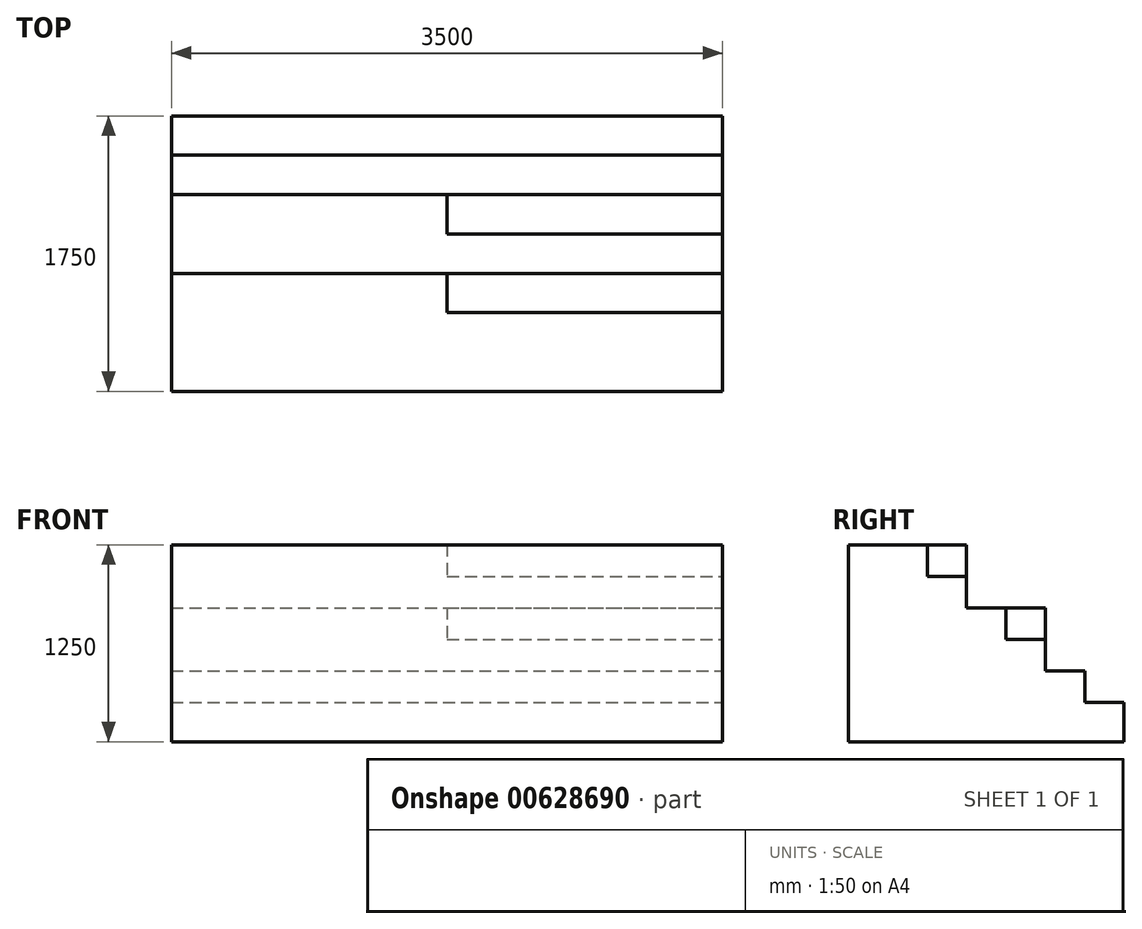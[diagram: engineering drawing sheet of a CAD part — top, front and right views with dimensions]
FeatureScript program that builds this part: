
annotation { "Feature Type Name" : "Feature", "Feature Type Description" : "" }
export const myFeature = defineFeature(function(context is Context, id is Id, definition is map)
    precondition{}
    {
        {
            var Q0;
            Q0=qCreatedBy(makeId("Top.planeOp"),FACE);
            var sketch = newSketch(context, id + "F0", { "sketchPlane" : qUnion([Q0])});
            skLineSegment(sketch, "E0.bottom", {"start": v(0, 0) * mm, "end": v(3500, 0) * mm});
            skLineSegment(sketch, "E0.top", {"start": v(0, 1500) * mm, "end": v(3500, 1500) * mm});
            skLineSegment(sketch, "E0.left", {"start": v(0, 0) * mm, "end": v(0, 1500) * mm});
            skLineSegment(sketch, "E0.right", {"start": v(3500, 0) * mm, "end": v(3500, 1500) * mm});
            skSolve(sketch);
        }
        {
            var Q0;
            Q0=makeQuery(id+"F0.imprint","IMPRINT",FACE,{"disambiguationData":[TD([[makeQuery(id+"F0.imprint","IMPRINT",EDGE,{"derivedFrom":sQuery(id+"F0.wireOp",EDGE,"E0.bottom")}),1.0]])]});
            extrude(context, id + "F1", {"entities" : qUnion([Q0]), "depth" : 250 * mm, "offsetDistance" : 25 * mm});
        }
        {
            var Q0;
            Q0=makeQuery(id+"F1.opExtrude","CAP_FACE",FACE,{"disambiguationData":[OSD([sQuery(id+"F0.wireOp",EDGE,"E0.bottom"),sQuery(id+"F0.wireOp",EDGE,"E0.top"),sQuery(id+"F0.wireOp",EDGE,"E0.left"),sQuery(id+"F0.wireOp",EDGE,"E0.right")])],"isStart":false});
            var sketch = newSketch(context, id + "F2", { "sketchPlane" : qUnion([Q0])});
            skLineSegment(sketch, "E1.bottom", {"start": v(0, 0) * mm, "end": v(3500, 0) * mm});
            skLineSegment(sketch, "E1.top", {"start": v(0, 1250) * mm, "end": v(3500, 1250) * mm});
            skLineSegment(sketch, "E1.left", {"start": v(0, 0) * mm, "end": v(0, 1250) * mm});
            skLineSegment(sketch, "E1.right", {"start": v(3500, 0) * mm, "end": v(3500, 1250) * mm});
            skLineSegment(sketch, "E2.bottom", {"start": v(0, 1250) * mm, "end": v(1750, 1250) * mm});
            skLineSegment(sketch, "E2.top", {"start": v(0, 1500) * mm, "end": v(1750, 1500) * mm});
            skLineSegment(sketch, "E2.left", {"start": v(0, 1250) * mm, "end": v(0, 1500) * mm});
            skLineSegment(sketch, "E2.right", {"start": v(1750, 1250) * mm, "end": v(1750, 1500) * mm});
            skSolve(sketch);
        }
        {
            var Q0;
            Q0=makeQuery(id+"F2.imprint","IMPRINT",FACE,{"disambiguationData":[TD([[makeQuery(id+"F2.imprint","IMPRINT",EDGE,{"derivedFrom":sQuery(id+"F2.wireOp",EDGE,"E1.bottom")}),1.0]])]});
            var Q1;
            Q1=makeQuery(id+"F2.imprint","IMPRINT",FACE,{"disambiguationData":[TD([[makeQuery(id+"F2.imprint","IMPRINT",EDGE,{"derivedFrom":sQuery(id+"F2.wireOp",EDGE,"E2.bottom")}),1.0]])]});
            extrude(context, id + "F3", {"entities" : qUnion([Q0, Q1]), "operationType" : NewBodyOperationType.ADD, "depth" : 200 * mm, "offsetDistance" : 25 * mm});
        }
        {
            var Q0;
            Q0=makeQuery(id+"F3.opExtrude","CAP_FACE",FACE,{"disambiguationData":[OSD([sQuery(id+"F2.wireOp",EDGE,"E1.bottom"),sQuery(id+"F2.wireOp",EDGE,"E1.top"),sQuery(id+"F2.wireOp",EDGE,"E1.left"),sQuery(id+"F2.wireOp",EDGE,"E1.right")])],"isStart":false});
            var sketch = newSketch(context, id + "F4", { "sketchPlane" : qUnion([Q0])});
            skLineSegment(sketch, "E3.bottom", {"start": v(0, 0) * mm, "end": v(1750, 0) * mm});
            skLineSegment(sketch, "E3.top", {"start": v(0, 500) * mm, "end": v(1750, 500) * mm});
            skLineSegment(sketch, "E3.left", {"start": v(0, 0) * mm, "end": v(0, 500) * mm});
            skLineSegment(sketch, "E3.right", {"start": v(1750, 0) * mm, "end": v(1750, 500) * mm});
            skLineSegment(sketch, "E4.bottom", {"start": v(1750, 0) * mm, "end": v(3500, 0) * mm});
            skLineSegment(sketch, "E4.top", {"start": v(1750, 250) * mm, "end": v(3500, 250) * mm});
            skLineSegment(sketch, "E4.left", {"start": v(1750, 0) * mm, "end": v(1750, 250) * mm});
            skLineSegment(sketch, "E4.right", {"start": v(3500, 0) * mm, "end": v(3500, 250) * mm});
            skLineSegment(sketch, "E5.left", {"start": v(1750, 500) * mm, "end": v(1750, 250) * mm});
            skSolve(sketch);
        }
        {
            var Q0;
            Q0 = qSketchRegion(id + "F4", true);
            extrude(context, id + "F5", {"entities" : qUnion([Q0]), "operationType" : NewBodyOperationType.ADD, "depth" : 800 * mm, "offsetDistance" : 25 * mm});
        }
        {
            var Q0;
            Q0=makeQuery(id+"F3.opExtrude","CAP_FACE",FACE,{"disambiguationData":[OSD([sQuery(id+"F2.wireOp",EDGE,"E1.bottom"),sQuery(id+"F2.wireOp",EDGE,"E1.top"),sQuery(id+"F2.wireOp",EDGE,"E1.left"),sQuery(id+"F2.wireOp",EDGE,"E1.right")])],"isStart":false});
            var sketch = newSketch(context, id + "F6", { "sketchPlane" : qUnion([Q0])});
            skLineSegment(sketch, "E6.bottom", {"start": v(1750, 500) * mm, "end": v(3500, 500) * mm});
            skLineSegment(sketch, "E6.top", {"start": v(1750, 250) * mm, "end": v(3500, 250) * mm});
            skLineSegment(sketch, "E6.left", {"start": v(1750, 500) * mm, "end": v(1750, 250) * mm});
            skLineSegment(sketch, "E6.right", {"start": v(3500, 500) * mm, "end": v(3500, 250) * mm});
            skSolve(sketch);
        }
        {
            var Q0;
            Q0=makeQuery(id+"F6.imprint","IMPRINT",FACE,{"disambiguationData":[TD([[makeQuery(id+"F6.imprint","IMPRINT",EDGE,{"derivedFrom":sQuery(id+"F6.wireOp",EDGE,"E6.bottom")}),-1.0]])]});
            extrude(context, id + "F7", {"entities" : qUnion([Q0]), "operationType" : NewBodyOperationType.ADD, "depth" : 600 * mm, "offsetDistance" : 25 * mm});
        }
        {
            var Q0;
            Q0=makeQuery(id+"F3.opExtrude","CAP_FACE",FACE,{"disambiguationData":[OSD([sQuery(id+"F2.wireOp",EDGE,"E1.bottom"),sQuery(id+"F2.wireOp",EDGE,"E1.top"),sQuery(id+"F2.wireOp",EDGE,"E1.left"),sQuery(id+"F2.wireOp",EDGE,"E1.right")])],"isStart":false});
            var sketch = newSketch(context, id + "F8", { "sketchPlane" : qUnion([Q0])});
            skLineSegment(sketch, "E7.bottom", {"start": v(0, 1000) * mm, "end": v(1750, 1000) * mm});
            skLineSegment(sketch, "E7.top", {"start": v(0, 500) * mm, "end": v(1750, 500) * mm});
            skLineSegment(sketch, "E7.left", {"start": v(0, 1000) * mm, "end": v(0, 500) * mm});
            skLineSegment(sketch, "E7.right", {"start": v(1750, 1000) * mm, "end": v(1750, 500) * mm});
            skLineSegment(sketch, "E8.bottom", {"start": v(1750, 750) * mm, "end": v(3500, 750) * mm});
            skLineSegment(sketch, "E8.top", {"start": v(1750, 500) * mm, "end": v(3500, 500) * mm});
            skLineSegment(sketch, "E8.left", {"start": v(1750, 750) * mm, "end": v(1750, 500) * mm});
            skLineSegment(sketch, "E8.right", {"start": v(3500, 750) * mm, "end": v(3500, 500) * mm});
            skSolve(sketch);
        }
        {
            var Q0;
            Q0 = qSketchRegion(id + "F8", true);
            extrude(context, id + "F9", {"entities" : qUnion([Q0]), "operationType" : NewBodyOperationType.ADD, "depth" : 400 * mm, "offsetDistance" : 25 * mm});
        }
        {
            var Q0;
            Q0=makeQuery(id+"F3.opExtrude","CAP_FACE",FACE,{"disambiguationData":[OSD([sQuery(id+"F2.wireOp",EDGE,"E1.bottom"),sQuery(id+"F2.wireOp",EDGE,"E1.top"),sQuery(id+"F2.wireOp",EDGE,"E1.left"),sQuery(id+"F2.wireOp",EDGE,"E1.right")])],"isStart":false});
            var sketch = newSketch(context, id + "F10", { "sketchPlane" : qUnion([Q0])});
            skLineSegment(sketch, "E9.bottom", {"start": v(1750, 1000) * mm, "end": v(3500, 1000) * mm});
            skLineSegment(sketch, "E9.top", {"start": v(1750, 750) * mm, "end": v(3500, 750) * mm});
            skLineSegment(sketch, "E9.left", {"start": v(1750, 1000) * mm, "end": v(1750, 750) * mm});
            skLineSegment(sketch, "E9.right", {"start": v(3500, 1000) * mm, "end": v(3500, 750) * mm});
            skSolve(sketch);
        }
        {
            var Q0;
            Q0=makeQuery(id+"F10.imprint","IMPRINT",FACE,{"disambiguationData":[TD([[makeQuery(id+"F10.imprint","IMPRINT",EDGE,{"derivedFrom":sQuery(id+"F10.wireOp",EDGE,"E9.bottom")}),-1.0]])]});
            extrude(context, id + "F11", {"entities" : qUnion([Q0]), "operationType" : NewBodyOperationType.ADD, "depth" : 200 * mm, "offsetDistance" : 25 * mm});
        }
        {
            var Q0;
            Q0=makeQuery(id+"F5.boolean.opBoolean","MERGE",FACE,{"derivedFrom":[makeQuery(id+"F3.boolean.opBoolean","MERGE",FACE,{"derivedFrom":[makeQuery(id+"F1.opExtrude","SWEPT_FACE",FACE,{"disambiguationData":[OSD([sQuery(id+"F0.wireOp",EDGE,"E0.bottom")])]}),makeQuery(id+"F3.opExtrude","SWEPT_FACE",FACE,{"disambiguationData":[OSD([sQuery(id+"F2.wireOp",EDGE,"E1.bottom")])]})]}),makeQuery(id+"F5.opExtrude","SWEPT_FACE",FACE,{"disambiguationData":[OSD([sQuery(id+"F4.wireOp",EDGE,"E3.bottom"),sQuery(id+"F4.wireOp",EDGE,"E4.bottom")])]})]});
            var sketch = newSketch(context, id + "F12", { "sketchPlane" : qUnion([Q0])});
            skLineSegment(sketch, "E10.bottom", {"start": v(0, 0) * mm, "end": v(3500, 0) * mm});
            skLineSegment(sketch, "E10.top", {"start": v(0, 1250) * mm, "end": v(3500, 1250) * mm});
            skLineSegment(sketch, "E10.left", {"start": v(0, 0) * mm, "end": v(0, 1250) * mm});
            skLineSegment(sketch, "E10.right", {"start": v(3500, 0) * mm, "end": v(3500, 1250) * mm});
            skSolve(sketch);
        }
        {
            var Q0;
            Q0=makeQuery(id+"F12.imprint","IMPRINT",FACE,{"disambiguationData":[TD([[makeQuery(id+"F12.imprint","IMPRINT",EDGE,{"derivedFrom":sQuery(id+"F12.wireOp",EDGE,"E10.bottom")}),1.0]])]});
            var sketch = newSketch(context, id + "F13", { "sketchPlane" : qUnion([Q0])});
            skSolve(sketch);
        }
        {
            var Q0;
            Q0=makeQuery(id+"F13.imprint","IMPRINT",FACE,{"disambiguationData":[TD([[makeQuery(id+"F13.imprint","IMPRINT",EDGE,{"derivedFrom":makeQuery(id+"F12.imprint","IMPRINT",EDGE,{"derivedFrom":sQuery(id+"F12.wireOp",EDGE,"E10.bottom")})}),1.0]])]});
            extrude(context, id + "F14", {"entities" : qUnion([Q0]), "operationType" : NewBodyOperationType.ADD, "depth" : 250 * mm, "offsetDistance" : 25 * mm});
        }
    });
